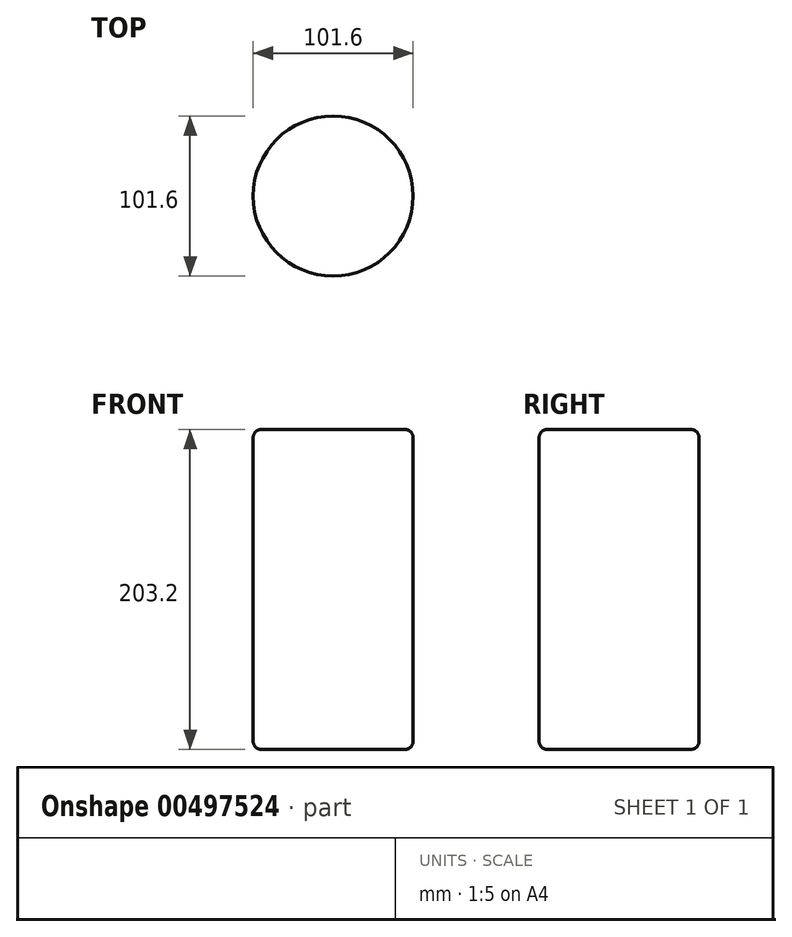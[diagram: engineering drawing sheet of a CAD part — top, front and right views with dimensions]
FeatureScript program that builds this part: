
annotation { "Feature Type Name" : "Feature", "Feature Type Description" : "" }
export const myFeature = defineFeature(function(context is Context, id is Id, definition is map)
    precondition{}
    {
        {
            var Q0;
            Q0=qCreatedBy(makeId("Top.planeOp"),FACE);
            var sketch = newSketch(context, id + "F0", { "sketchPlane" : qUnion([Q0])});
            skCircle(sketch, "E0", {"center": v(0, 0) * mm, "radius": 50.8 * mm});
            skSolve(sketch);
        }
        {
            var Q0;
            Q0 = qSketchRegion(id + "F0", true);
            extrude(context, id + "F1", {"entities" : qUnion([Q0]), "depth" : 203.2 * mm});
        }
        {
            var Q0;
            Q0=makeQuery(id+"F1.opExtrude","CAP_FACE",FACE,{"disambiguationData":[OSD([sQuery(id+"F0.wireOp",EDGE,"E0")])],"isStart":true});
            var Q1;
            Q1=makeQuery(id+"F1.opExtrude","CAP_EDGE",EDGE,{"disambiguationData":[OSD([sQuery(id+"F0.wireOp",EDGE,"E0")])],"isStart":false});
            var Q2;
            Q2=makeQuery(id+"F1.opExtrude","SWEPT_FACE",FACE,{"disambiguationData":[OSD([sQuery(id+"F0.wireOp",EDGE,"E0")])]});
            fillet(context, id + "F2", {"entities" : qUnion([Q0, Q1, Q2]), "radius" : 5.08 * mm, "tangentPropagation" : true, "allowEdgeOverflow" : false});
        }
    });
